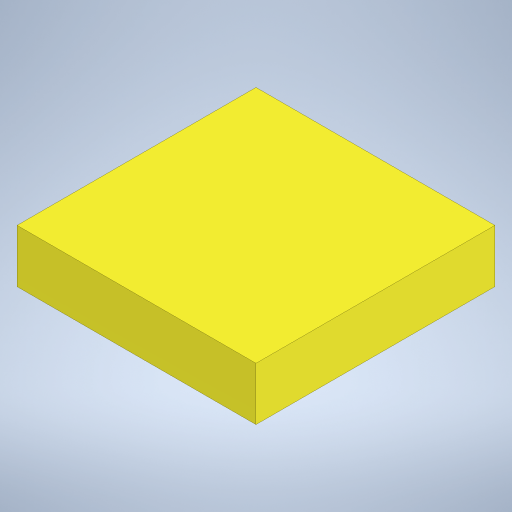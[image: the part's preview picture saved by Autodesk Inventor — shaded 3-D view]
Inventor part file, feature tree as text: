
AUTODESK INVENTOR PART (.ipt)
format: ipt  version: 2024 (Build 280153000, 153)  size: 185,856 bytes
history: native  units: mm
features: extrude x1, sketch x1
ambient origin geometry x8: Origin, YZ Plane, XZ Plane, XY Plane, X Axis, Y Axis, Z Axis, Center Point
bodies: Solid1 (feature_tree)
feature tree (2):
  extrude  "Extrusion1"  Depth=9.0mm
  sketch  "Sketch1"  dims[d0=9.0mm d1=9.0mm d2=2.0mm d3=0.0mm]
